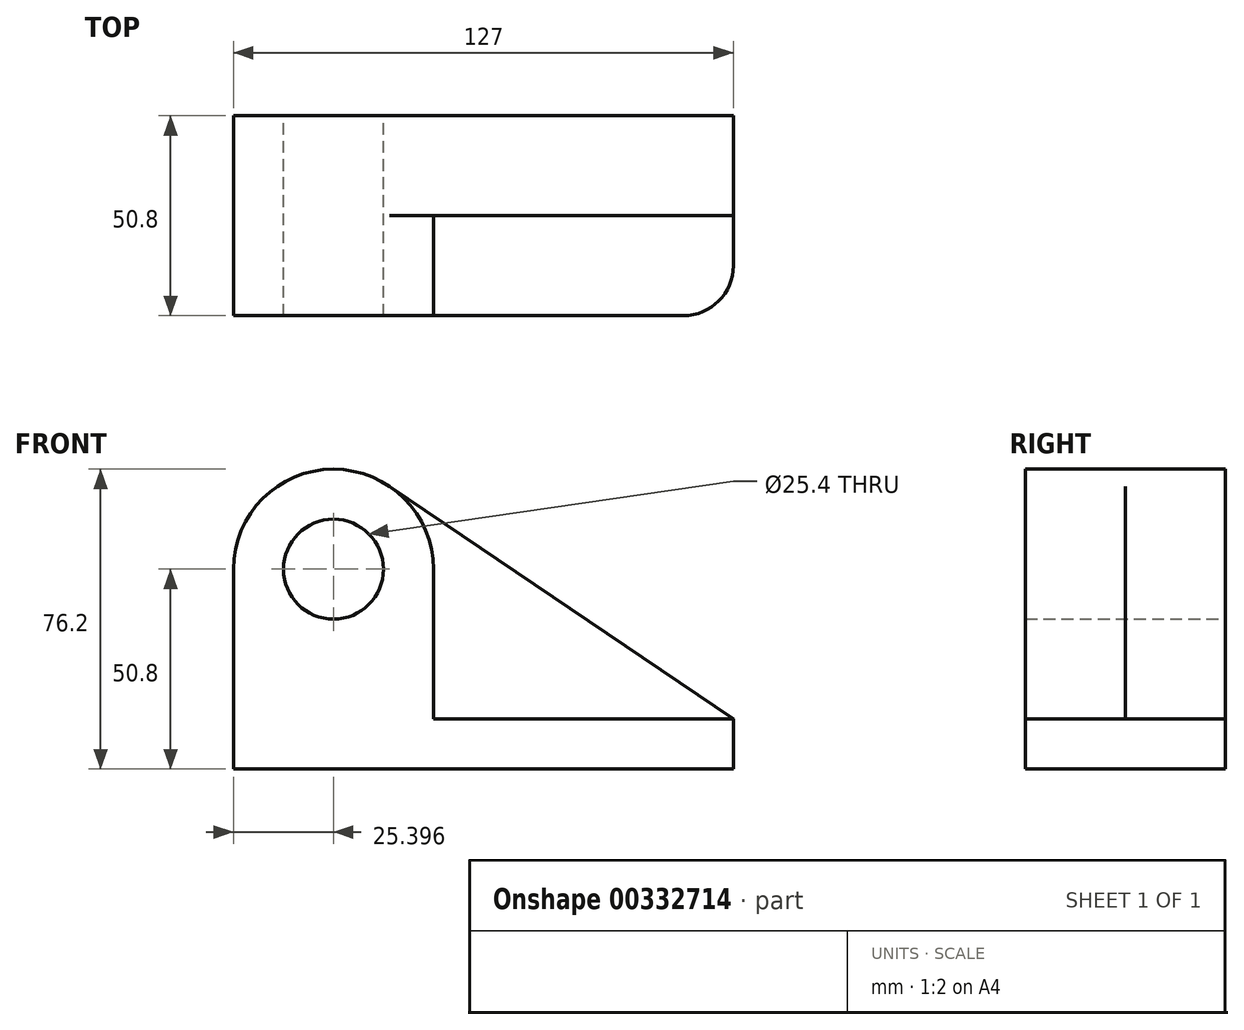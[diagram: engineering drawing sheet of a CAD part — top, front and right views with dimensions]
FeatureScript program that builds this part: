
annotation { "Feature Type Name" : "Feature", "Feature Type Description" : "" }
export const myFeature = defineFeature(function(context is Context, id is Id, definition is map)
    precondition{}
    {
        {
            var Q0;
            Q0=qCreatedBy(makeId("Front.planeOp"),FACE);
            var sketch = newSketch(context, id + "F0", { "sketchPlane" : qUnion([Q0])});
            skCircle(sketch, "E0", {"center": v(-47.24, 50.8) * mm, "radius": 12.7 * mm});
            skArc(sketch, "E1", {"start": v(-33, 71.83) * mm, "mid": v(-59.15, 73.24) * mm, "end": v(-72.64, 50.8) * mm});
            skLineSegment(sketch, "E2", {"start": v(-72.64, 50.8) * mm, "end": v(-72.64, 0) * mm});
            skLineSegment(sketch, "E3", {"start": v(-72.64, 0) * mm, "end": v(54.36, 0) * mm});
            skLineSegment(sketch, "E4", {"start": v(54.36, 0) * mm, "end": v(54.36, 12.7) * mm});
            skLineSegment(sketch, "E5", {"start": v(54.36, 12.7) * mm, "end": v(-33, 71.83) * mm});
            skSolve(sketch);
        }
        {
            var Q0;
            Q0=makeQuery(id+"F0.imprint","IMPRINT",FACE,{"disambiguationData":[TD([[makeQuery(id+"F0.imprint","IMPRINT",EDGE,{"derivedFrom":sQuery(id+"F0.wireOp",EDGE,"E0")}),-1.0]])]});
            extrude(context, id + "F1", {"entities" : qUnion([Q0]), "depth" : 25.4 * mm});
        }
        {
            var Q0;
            Q0=makeQuery(id+"F1.opExtrude","CAP_FACE",FACE,{"disambiguationData":[OSD([sQuery(id+"F0.wireOp",EDGE,"E0"),sQuery(id+"F0.wireOp",EDGE,"E1"),sQuery(id+"F0.wireOp",EDGE,"E2"),sQuery(id+"F0.wireOp",EDGE,"E3"),sQuery(id+"F0.wireOp",EDGE,"E4"),sQuery(id+"F0.wireOp",EDGE,"E5")])],"isStart":false});
            var sketch = newSketch(context, id + "F2", { "sketchPlane" : qUnion([Q0])});
            skCircle(sketch, "E6", {"center": v(-47.24, 50.8) * mm, "radius": 12.7 * mm});
            skLineSegment(sketch, "E7.bottom", {"start": v(54.36, 12.7) * mm, "end": v(-21.84, 12.7) * mm});
            skLineSegment(sketch, "E7.top", {"start": v(54.36, 0) * mm, "end": v(-72.64, 0) * mm});
            skLineSegment(sketch, "E7.left", {"start": v(54.36, 12.7) * mm, "end": v(54.36, 0) * mm});
            skLineSegment(sketch, "E7.right", {"start": v(-72.64, 12.7) * mm, "end": v(-72.64, 0) * mm});
            skLineSegment(sketch, "E8", {"start": v(-21.84, 50.8) * mm, "end": v(-21.84, 12.7) * mm});
            skArc(sketch, "E9", {"start": v(-21.84, 50.8) * mm, "mid": v(-47.24, 76.2) * mm, "end": v(-72.64, 50.8) * mm});
            skSolve(sketch);
        }
        {
            var Q0;
            Q0=makeQuery(id+"F2.imprint","IMPRINT",FACE,{"disambiguationData":[TD([[makeQuery(id+"F2.imprint","IMPRINT",EDGE,{"derivedFrom":sQuery(id+"F2.wireOp",EDGE,"E6")}),-1.0]])]});
            extrude(context, id + "F3", {"entities" : qUnion([Q0]), "operationType" : NewBodyOperationType.ADD, "depth" : 25.4 * mm});
        }
        {
            var Q0;
            Q0=makeQuery(id+"F3.opExtrude","CAP_EDGE",EDGE,{"disambiguationData":[OSD([sQuery(id+"F2.wireOp",EDGE,"E7.left")])],"isStart":false});
            fillet(context, id + "F4", {"entities" : qUnion([Q0]), "radius" : 12.7 * mm, "tangentPropagation" : true, "allowEdgeOverflow" : false});
        }
    });
